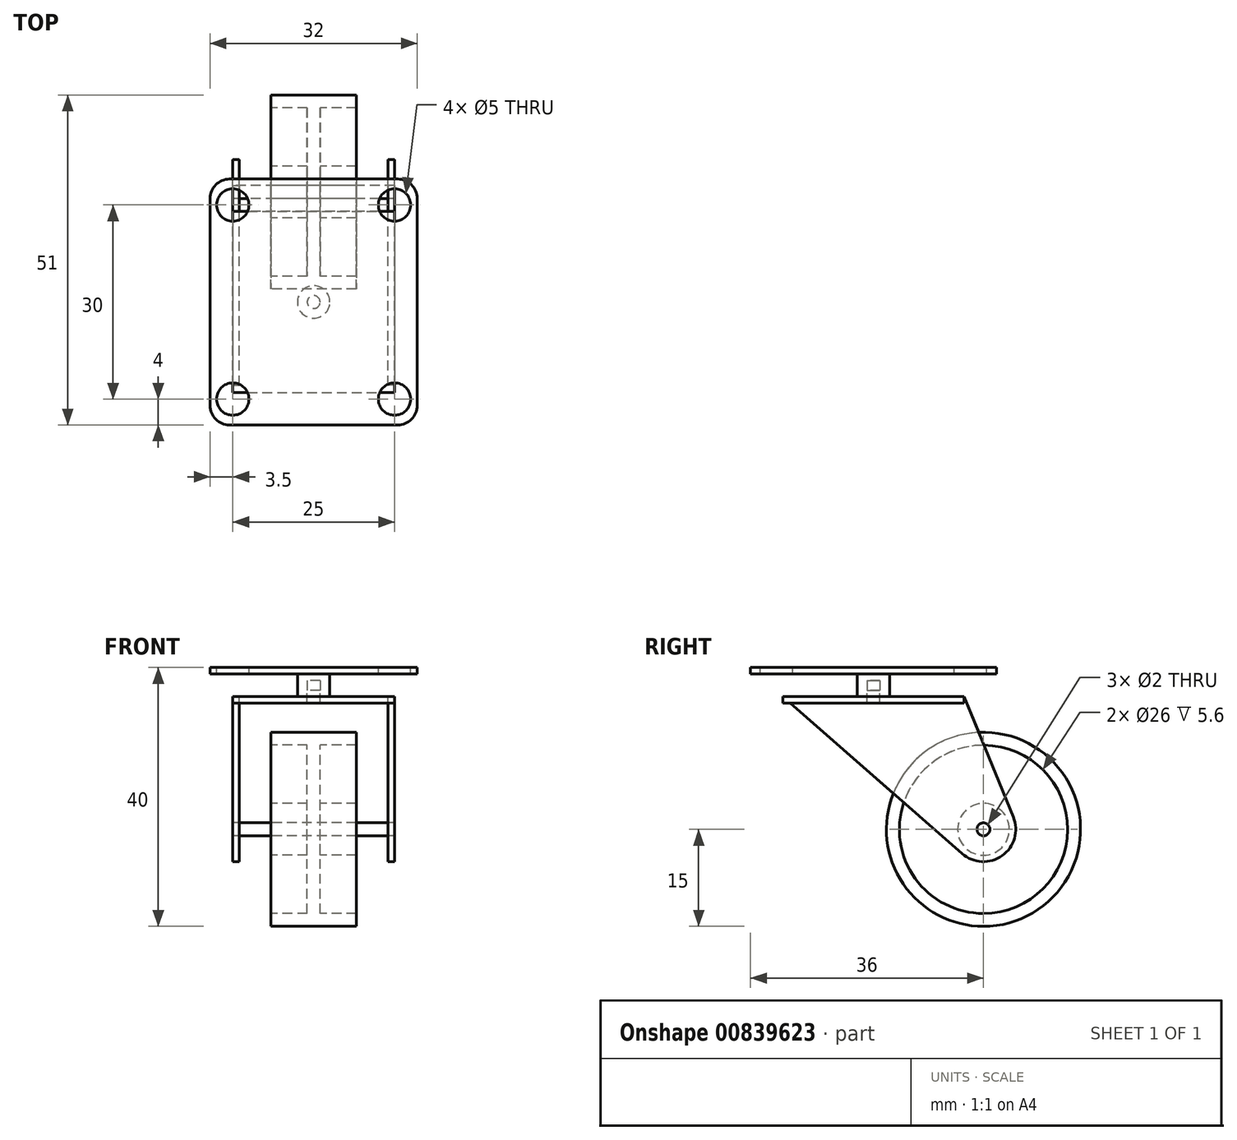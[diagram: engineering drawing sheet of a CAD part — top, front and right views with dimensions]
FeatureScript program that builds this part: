
annotation { "Feature Type Name" : "Feature", "Feature Type Description" : "" }
export const myFeature = defineFeature(function(context is Context, id is Id, definition is map)
    precondition{}
    {
        {
            var Q0;
            Q0=qCreatedBy(makeId("Right.planeOp"),FACE);
            var sketch = newSketch(context, id + "F0", { "sketchPlane" : qUnion([Q0])});
            skCircle(sketch, "E0", {"center": v(0, 0) * mm, "radius": 15 * mm});
            skCircle(sketch, "E1", {"center": v(0, 0) * mm, "radius": 4 * mm});
            skCircle(sketch, "E2", {"center": v(0, 0) * mm, "radius": 13 * mm});
            skCircle(sketch, "E3", {"center": v(0, 0) * mm, "radius": 1 * mm});
            skSolve(sketch);
        }
        {
            var Q0;
            Q0=makeQuery(id+"F0.imprint","IMPRINT",FACE,{"disambiguationData":[TD([[makeQuery(id+"F0.imprint","IMPRINT",EDGE,{"derivedFrom":sQuery(id+"F0.wireOp",EDGE,"E1")}),-1.0]])]});
            extrude(context, id + "F1", {"entities" : qUnion([Q0]), "endBound" : BoundingType.SYMMETRIC, "depth" : 2 * mm, "offsetDistance" : 25 * mm});
        }
        {
            var Q0;
            Q0=makeQuery(id+"F0.imprint","IMPRINT",FACE,{"disambiguationData":[TD([[makeQuery(id+"F0.imprint","IMPRINT",EDGE,{"derivedFrom":sQuery(id+"F0.wireOp",EDGE,"E0")}),1.0]])]});
            var Q1;
            Q1=makeQuery(id+"F0.imprint","IMPRINT",FACE,{"disambiguationData":[TD([[makeQuery(id+"F0.imprint","IMPRINT",EDGE,{"derivedFrom":sQuery(id+"F0.wireOp",EDGE,"E1")}),1.0]])]});
            extrude(context, id + "F2", {"entities" : qUnion([Q0, Q1]), "operationType" : NewBodyOperationType.ADD, "endBound" : BoundingType.SYMMETRIC, "depth" : 13.2 * mm, "offsetDistance" : 25 * mm});
        }
        {
            var Q0;
            Q0=qCreatedBy(makeId("Top.planeOp"),FACE);
            cPlane(context, id + "F3", {"entities" : qUnion([Q0]), "cplaneType" : CPlaneType.OFFSET, "offset" : 20 * mm, "width" : 150 * mm, "height" : 150 * mm});
        }
        {
            var Q0;
            Q0=qCreatedBy(id+"F3.planeOp",FACE);
            var sketch = newSketch(context, id + "F4", { "sketchPlane" : qUnion([Q0])});
            skLineSegment(sketch, "E4", {"start": v(21.36, 0) * mm, "end": v(-21.36, 0) * mm, "construction": true});
            skLineSegment(sketch, "E5", {"start": v(-21.21, -3) * mm, "end": v(20.36, -3) * mm, "construction": true});
            skLineSegment(sketch, "E6", {"start": v(-21.21, -3) * mm, "end": v(-21.21, -31) * mm, "construction": true});
            skLineSegment(sketch, "E7", {"start": v(27.4, -31) * mm, "end": v(-21.21, -31) * mm, "construction": true});
            skLineSegment(sketch, "E8.bottom", {"start": v(-12.5, -3) * mm, "end": v(12.5, -3) * mm});
            skLineSegment(sketch, "E8.top", {"start": v(-12.5, -31) * mm, "end": v(12.5, -31) * mm});
            skLineSegment(sketch, "E8.left", {"start": v(-12.5, -3) * mm, "end": v(-12.5, -31) * mm});
            skLineSegment(sketch, "E8.right", {"start": v(12.5, -3) * mm, "end": v(12.5, -31) * mm});
            skCircle(sketch, "E9", {"center": v(0, -17) * mm, "radius": 1 * mm});
            skSolve(sketch);
        }
        {
            var Q0;
            Q0=makeQuery(id+"F4.imprint","IMPRINT",FACE,{"disambiguationData":[TD([[makeQuery(id+"F4.imprint","IMPRINT",EDGE,{"derivedFrom":sQuery(id+"F4.wireOp",EDGE,"E8.bottom")}),-1.0]])]});
            extrude(context, id + "F5", {"entities" : qUnion([Q0]), "endBound" : BoundingType.SYMMETRIC, "oppositeDirection" : true, "depth" : 1 * mm, "offsetDistance" : 25 * mm});
        }
        {
            var Q0;
            Q0=qCreatedBy(makeId("Right.planeOp"),FACE);
            cPlane(context, id + "F6", {"entities" : qUnion([Q0]), "cplaneType" : CPlaneType.OFFSET, "offset" : 11.5 * mm, "width" : 150 * mm, "height" : 150 * mm});
        }
        {
            var Q0;
            Q0=qCreatedBy(id+"F6.planeOp",FACE);
            var sketch = newSketch(context, id + "F7", { "sketchPlane" : qUnion([Q0])});
            skLineSegment(sketch, "E10.0", {"start": v(-31, 20.5) * mm, "end": v(-3, 20.5) * mm});
            skCircle(sketch, "E11.0", {"center": v(0, 0) * mm, "radius": 1 * mm});
            skArc(sketch, "E12", {"start": v(-3.3, -3.76) * mm, "mid": v(2.9, -4.07) * mm, "end": v(4.63, 1.9) * mm});
            skLineSegment(sketch, "E13", {"start": v(-3, 20.5) * mm, "end": v(4.63, 1.9) * mm});
            skLineSegment(sketch, "E14", {"start": v(-31, 20.5) * mm, "end": v(-3.3, -3.76) * mm});
            skSolve(sketch);
        }
        {
            var Q0;
            Q0=makeQuery(id+"F7.imprint","IMPRINT",FACE,{"disambiguationData":[TD([[makeQuery(id+"F7.imprint","IMPRINT",EDGE,{"derivedFrom":sQuery(id+"F7.wireOp",EDGE,"E10.0")}),1.0]])]});
            var Q1;
            Q1=makeQuery(id+"F7.imprint","IMPRINT",FACE,{"disambiguationData":[TD([[makeQuery(id+"F7.imprint","IMPRINT",EDGE,{"derivedFrom":sQuery(id+"F7.wireOp",EDGE,"E10.0")}),-1.0]])]});
            extrude(context, id + "F8", {"entities" : qUnion([Q0, Q1]), "operationType" : NewBodyOperationType.ADD, "depth" : 1 * mm, "offsetDistance" : 25 * mm});
        }
        {
            var Q0;
            Q0=makeQuery(id+"F5.opExtrude","SWEPT_BODY",BODY,{"disambiguationData":[OSD([sQuery(id+"F4.wireOp",EDGE,"E8.bottom"),sQuery(id+"F4.wireOp",EDGE,"E8.top"),sQuery(id+"F4.wireOp",EDGE,"E8.left"),sQuery(id+"F4.wireOp",EDGE,"E8.right")])]});
            var Q1;
            Q1=qCreatedBy(makeId("Right.planeOp"),FACE);
            mirror(context, id + "F9", {"operationType" : NewBodyOperationType.ADD, "entities" : qUnion([Q0]), "mirrorPlane" : qUnion([Q1])});
        }
        {
            var Q0;
            Q0=qCreatedBy(makeId("Top.planeOp"),FACE);
            cPlane(context, id + "F10", {"entities" : qUnion([Q0]), "cplaneType" : CPlaneType.OFFSET, "offset" : 25 * mm, "width" : 150 * mm, "height" : 150 * mm});
        }
        {
            var Q0;
            Q0=qCreatedBy(id+"F10.planeOp",FACE);
            var sketch = newSketch(context, id + "F11", { "sketchPlane" : qUnion([Q0])});
            skCircle(sketch, "E15.0", {"center": v(0, -17) * mm, "radius": 1 * mm});
            skLineSegment(sketch, "E16", {"start": v(19.03, -17) * mm, "end": v(-22.85, -17) * mm, "construction": true});
            skLineSegment(sketch, "E17.bottom", {"start": v(-13, -36) * mm, "end": v(13, -36) * mm});
            skLineSegment(sketch, "E17.top", {"start": v(-13, 2) * mm, "end": v(13, 2) * mm});
            skLineSegment(sketch, "E17.left", {"start": v(-16, -33) * mm, "end": v(-16, -1) * mm});
            skLineSegment(sketch, "E17.right", {"start": v(16, -33) * mm, "end": v(16, -1) * mm});
            skCircle(sketch, "E18", {"center": v(-12.5, -2) * mm, "radius": 2.5 * mm});
            skCircle(sketch, "E19.MirrorC", {"center": v(12.5, -2) * mm, "radius": 2.5 * mm});
            skCircle(sketch, "E20.MirrorC", {"center": v(-12.5, -32) * mm, "radius": 2.5 * mm});
            skCircle(sketch, "E21.MirrorC", {"center": v(12.5, -32) * mm, "radius": 2.5 * mm});
            skPoint(sketch, "E22.visualSharp", {"position": v(-16, -36) * mm});
            skArc(sketch, "E22.filletArc", {"start": v(-16, -33) * mm, "mid": v(-15.12, -35.12) * mm, "end": v(-13, -36) * mm});
            skPoint(sketch, "E23.visualSharp", {"position": v(16, -36) * mm});
            skArc(sketch, "E23.filletArc", {"start": v(13, -36) * mm, "mid": v(15.12, -35.12) * mm, "end": v(16, -33) * mm});
            skPoint(sketch, "E24.visualSharp", {"position": v(16, 2) * mm});
            skArc(sketch, "E24.filletArc", {"start": v(16, -1) * mm, "mid": v(15.12, 1.12) * mm, "end": v(13, 2) * mm});
            skPoint(sketch, "E25.visualSharp", {"position": v(-16, 2) * mm});
            skArc(sketch, "E25.filletArc", {"start": v(-13, 2) * mm, "mid": v(-15.12, 1.12) * mm, "end": v(-16, -1) * mm});
            skSolve(sketch);
        }
        {
            var Q0;
            Q0=makeQuery(id+"F11.imprint","IMPRINT",FACE,{"disambiguationData":[TD([[makeQuery(id+"F11.imprint","IMPRINT",EDGE,{"derivedFrom":sQuery(id+"F11.wireOp",EDGE,"E17.bottom")}),1.0]])]});
            extrude(context, id + "F12", {"entities" : qUnion([Q0]), "oppositeDirection" : true, "depth" : 1 * mm, "offsetDistance" : 25 * mm});
        }
        {
            var Q0;
            Q0=makeQuery(id+"F5.opExtrude","CAP_FACE",FACE,{"disambiguationData":[OSD([sQuery(id+"F4.wireOp",EDGE,"E8.bottom"),sQuery(id+"F4.wireOp",EDGE,"E8.top"),sQuery(id+"F4.wireOp",EDGE,"E8.left"),sQuery(id+"F4.wireOp",EDGE,"E8.right"),sQuery(id+"F4.wireOp",EDGE,"E9")])],"isStart":true});
            var sketch = newSketch(context, id + "F13", { "sketchPlane" : qUnion([Q0])});
            skCircle(sketch, "E26.0", {"center": v(0, -17) * mm, "radius": 1 * mm});
            skCircle(sketch, "E27", {"center": v(0, -17) * mm, "radius": 2.5 * mm});
            skSolve(sketch);
        }
        {
            var Q0;
            Q0=makeQuery(id+"F13.imprint","IMPRINT",FACE,{"disambiguationData":[TD([[makeQuery(id+"F13.imprint","IMPRINT",EDGE,{"derivedFrom":sQuery(id+"F13.wireOp",EDGE,"E26.0")}),1.0]])]});
            extrude(context, id + "F14", {"entities" : qUnion([Q0]), "endBound" : BoundingType.SYMMETRIC, "oppositeDirection" : true, "depth" : 2 * mm, "offsetDistance" : 25 * mm});
        }
        {
            var Q0;
            Q0=makeQuery(id+"F13.imprint","IMPRINT",FACE,{"disambiguationData":[TD([[makeQuery(id+"F13.imprint","IMPRINT",EDGE,{"derivedFrom":sQuery(id+"F13.wireOp",EDGE,"E26.0")}),-1.0]])]});
            extrude(context, id + "F15", {"entities" : qUnion([Q0]), "depth" : 3.5 * mm, "offsetDistance" : 25 * mm});
        }
        {
            var Q0;
            Q0=makeQuery(id+"F15.opExtrude","CAP_FACE",FACE,{"disambiguationData":[OSD([sQuery(id+"F13.wireOp",EDGE,"E26.0"),sQuery(id+"F13.wireOp",EDGE,"E27")])],"isStart":false});
            var sketch = newSketch(context, id + "F16", { "sketchPlane" : qUnion([Q0])});
            skCircle(sketch, "E28.0", {"center": v(0, -17) * mm, "radius": 1 * mm});
            skSolve(sketch);
        }
        {
            var Q0;
            Q0=makeQuery(id+"F16.imprint","IMPRINT",FACE,{"disambiguationData":[TD([[makeQuery(id+"F16.imprint","IMPRINT",EDGE,{"derivedFrom":sQuery(id+"F16.wireOp",EDGE,"E28.0")}),1.0]])]});
            extrude(context, id + "F17", {"entities" : qUnion([Q0]), "operationType" : NewBodyOperationType.ADD, "endBound" : BoundingType.SYMMETRIC, "depth" : 2 * mm, "offsetDistance" : 25 * mm});
        }
        {
            var Q0;
            Q0=qCreatedBy(makeId("Right.planeOp"),FACE);
            var sketch = newSketch(context, id + "F18", { "sketchPlane" : qUnion([Q0])});
            skCircle(sketch, "E29", {"center": v(0, 0) * mm, "radius": 1 * mm});
            skSolve(sketch);
        }
        {
            var Q0;
            Q0=makeQuery(id+"F18.imprint","IMPRINT",FACE,{"disambiguationData":[TD([[makeQuery(id+"F18.imprint","IMPRINT",EDGE,{"derivedFrom":sQuery(id+"F18.wireOp",EDGE,"E29")}),1.0]])]});
            extrude(context, id + "F19", {"entities" : qUnion([Q0]), "endBound" : BoundingType.SYMMETRIC, "depth" : 25 * mm, "offsetDistance" : 25 * mm});
        }
    });
